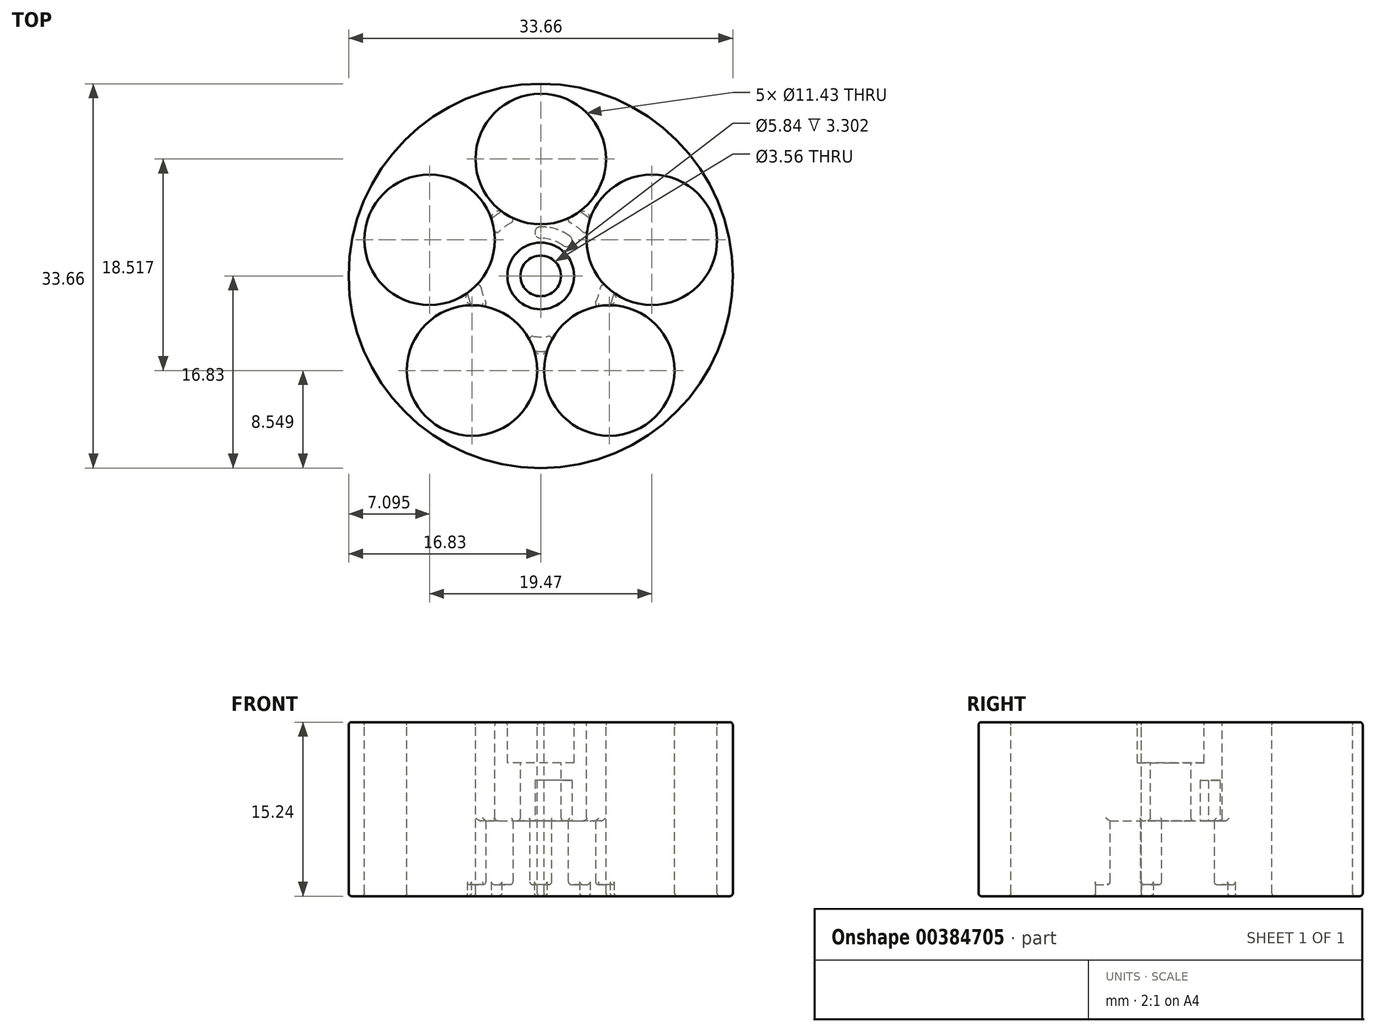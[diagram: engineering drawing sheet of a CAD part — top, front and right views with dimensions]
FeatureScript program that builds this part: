
annotation { "Feature Type Name" : "Feature", "Feature Type Description" : "" }
export const myFeature = defineFeature(function(context is Context, id is Id, definition is map)
    precondition{}
    {
        {
            var Q0;
            Q0=qCreatedBy(makeId("Top.planeOp"),FACE);
            var sketch = newSketch(context, id + "F0", { "sketchPlane" : qUnion([Q0])});
            skCircle(sketch, "E0", {"center": v(0, 0) * mm, "radius": 16.83 * mm});
            skSolve(sketch);
        }
        {
            var Q0;
            Q0=qSketchRegion(id+"F0",true);
            extrude(context, id + "F1", {"entities" : qUnion([Q0]), "depth" : 15.24 * mm, "offsetDistance" : 25.4 * mm});
        }
        {
            var Q0;
            Q0=makeQuery(id+"F1.opExtrude","CAP_FACE",FACE,{"disambiguationData":[OSD([sQuery(id+"F0.wireOp",EDGE,"E0")])],"isStart":false});
            var sketch = newSketch(context, id + "F2", { "sketchPlane" : qUnion([Q0])});
            skCircle(sketch, "E1", {"center": v(0, 10.24) * mm, "radius": 5.72 * mm});
            skCircle(sketch, "E2.1.0", {"center": v(-9.74, 3.16) * mm, "radius": 5.72 * mm});
            skCircle(sketch, "E2.2.0", {"center": v(-6.02, -8.28) * mm, "radius": 5.72 * mm});
            skCircle(sketch, "E2.3.0", {"center": v(6.02, -8.28) * mm, "radius": 5.72 * mm});
            skCircle(sketch, "E2.4.0", {"center": v(9.74, 3.16) * mm, "radius": 5.72 * mm});
            skPoint(sketch, "E2.center", {"position": v(0, 0) * mm});
            skSolve(sketch);
        }
        {
            var Q0;
            Q0=qSketchRegion(id+"F2",true);
            extrude(context, id + "F3", {"entities" : qUnion([Q0]), "operationType" : NewBodyOperationType.REMOVE, "oppositeDirection" : true, "depth" : 15.24 * mm});
        }
        {
            var Q0;
            Q0=makeQuery(id+"F1.opExtrude","CAP_FACE",FACE,{"disambiguationData":[OSD([sQuery(id+"F0.wireOp",EDGE,"E0")])],"isStart":true});
            var sketch = newSketch(context, id + "F4", { "sketchPlane" : qUnion([Q0])});
            skCircle(sketch, "E3", {"center": v(0, 0) * mm, "radius": 5.33 * mm});
            skSolve(sketch);
        }
        {
            var Q0;
            Q0=qSketchRegion(id+"F4",true);
            extrude(context, id + "F5", {"entities" : qUnion([Q0]), "operationType" : NewBodyOperationType.REMOVE, "oppositeDirection" : true, "depth" : 6.6 * mm, "offsetDistance" : 25.4 * mm});
        }
        {
            var Q0;
            Q0=makeQuery(id+"F1.opExtrude","CAP_FACE",FACE,{"disambiguationData":[OSD([sQuery(id+"F0.wireOp",EDGE,"E0")])],"isStart":false});
            var sketch = newSketch(context, id + "F6", { "sketchPlane" : qUnion([Q0])});
            skCircle(sketch, "E4", {"center": v(0, 0) * mm, "radius": 2.92 * mm});
            skSolve(sketch);
        }
        {
            var Q0;
            Q0=qSketchRegion(id+"F6",true);
            extrude(context, id + "F7", {"entities" : qUnion([Q0]), "operationType" : NewBodyOperationType.REMOVE, "oppositeDirection" : true, "depth" : 3.56 * mm});
        }
        {
            var Q0;
            Q0=makeQuery(id+"F7.boolean.opBoolean","COPY",FACE,{"derivedFrom":makeQuery(id+"F7.opExtrude","CAP_FACE",FACE,{"disambiguationData":[OSD([sQuery(id+"F6.wireOp",EDGE,"E4")])],"isStart":false})});
            var sketch = newSketch(context, id + "F8", { "sketchPlane" : qUnion([Q0])});
            skCircle(sketch, "E5", {"center": v(0, 0) * mm, "radius": 1.78 * mm});
            skSolve(sketch);
        }
        {
            var Q0;
            Q0=qSketchRegion(id+"F8",true);
            extrude(context, id + "F9", {"entities" : qUnion([Q0]), "operationType" : NewBodyOperationType.REMOVE, "oppositeDirection" : true, "depth" : 25.4 * mm});
        }
        {
            var Q0;
            Q0=makeQuery(id+"F1.opExtrude","CAP_FACE",FACE,{"disambiguationData":[OSD([sQuery(id+"F0.wireOp",EDGE,"E0")])],"isStart":true});
            var sketch = newSketch(context, id + "F10", { "sketchPlane" : qUnion([Q0])});
            skSolve(sketch);
        }
        {
            var Q0;
            {var subQ0=sQuery(id+"F0.wireOp",EDGE,"E0");Q0=makeQuery(id+"F10.imprint","IMPRINT",FACE,{"disambiguationData":[TD([[makeQuery(id+"F10.imprint","IMPRINT",EDGE,{"derivedFrom":makeQuery(id+"F1.opExtrude","CAP_EDGE",EDGE,{"disambiguationData":[OSD([subQ0])],"isStart":true})}),-1.0]])]});}
            var sketch = newSketch(context, id + "F11", { "sketchPlane" : qUnion([Q0])});
            skCircle(sketch, "E6", {"center": v(0, 0) * mm, "radius": 6.6 * mm});
            skSolve(sketch);
        }
        {
            var Q0;
            Q0=qSketchRegion(id+"F11",true);
            extrude(context, id + "F12", {"entities" : qUnion([Q0]), "operationType" : NewBodyOperationType.REMOVE, "oppositeDirection" : true, "depth" : 1.02 * mm, "offsetDistance" : 25.4 * mm});
        }
        {
            var Q0;
            Q0=qCreatedBy(makeId("Top.planeOp"),FACE);
            var sketch = newSketch(context, id + "F13", { "sketchPlane" : qUnion([Q0])});
            skArc(sketch, "E7", {"start": v(0, 4.32) * mm, "mid": v(-0.5, 3.81) * mm, "end": v(0, 3.3) * mm});
            skArc(sketch, "E8", {"start": v(1.94, 2.67) * mm, "mid": v(2.65, 2.78) * mm, "end": v(2.54, 3.5) * mm});
            skArc(sketch, "E9", {"start": v(1.94, 2.67) * mm, "mid": v(1.02, 3.14) * mm, "end": v(0, 3.3) * mm});
            skArc(sketch, "E10", {"start": v(2.54, 3.5) * mm, "mid": v(1.33, 4.1) * mm, "end": v(0, 4.32) * mm});
            skPoint(sketch, "E11.trimOffspring.end.orphan", {"position": v(6.02, -8.28) * mm});
            skSolve(sketch);
        }
        {
            var Q0;
            Q0=qSketchRegion(id+"F13",true);
            extrude(context, id + "F14", {"entities" : qUnion([Q0]), "operationType" : NewBodyOperationType.REMOVE, "depth" : 10.16 * mm, "offsetDistance" : 25.4 * mm});
        }
        {
            var Q0;
            Q0=makeQuery(id+"F1.opExtrude","CAP_FACE",FACE,{"disambiguationData":[OSD([sQuery(id+"F0.wireOp",EDGE,"E0")])],"isStart":false});
            var Q1;
            Q1=makeQuery(id+"F1.opExtrude","CAP_FACE",FACE,{"disambiguationData":[OSD([sQuery(id+"F0.wireOp",EDGE,"E0")])],"isStart":true});
            fillet(context, id + "F15", {"entities" : qUnion([Q0, Q1]), "radius" : 0.25 * mm, "tangentPropagation" : true, "allowEdgeOverflow" : false});
        }
        {
            var Q0;
            Q0=makeQuery(id+"F5.boolean.opBoolean","INTERSECT",EDGE,{"disambiguationData":[OD(0.0)],"derivedFrom":[makeQuery(id+"F3.boolean.opBoolean","COPY",FACE,{"derivedFrom":makeQuery(id+"F3.opExtrude","SWEPT_FACE",FACE,{"disambiguationData":[OSD([sQuery(id+"F2.wireOp",EDGE,"E2.3.0")])]})}),makeQuery(id+"F5.opExtrude","SWEPT_FACE",FACE,{"disambiguationData":[OSD([sQuery(id+"F4.wireOp",EDGE,"E3")])]})]});
            var Q1;
            Q1=makeQuery(id+"F5.boolean.opBoolean","INTERSECT",EDGE,{"disambiguationData":[OD(1.0)],"derivedFrom":[makeQuery(id+"F3.boolean.opBoolean","COPY",FACE,{"derivedFrom":makeQuery(id+"F3.opExtrude","SWEPT_FACE",FACE,{"disambiguationData":[OSD([sQuery(id+"F2.wireOp",EDGE,"E2.2.0")])]})}),makeQuery(id+"F5.opExtrude","SWEPT_FACE",FACE,{"disambiguationData":[OSD([sQuery(id+"F4.wireOp",EDGE,"E3")])]})]});
            var Q2;
            Q2=makeQuery(id+"F5.boolean.opBoolean","INTERSECT",EDGE,{"disambiguationData":[OD(0.0)],"derivedFrom":[makeQuery(id+"F3.boolean.opBoolean","COPY",FACE,{"derivedFrom":makeQuery(id+"F3.opExtrude","SWEPT_FACE",FACE,{"disambiguationData":[OSD([sQuery(id+"F2.wireOp",EDGE,"E2.2.0")])]})}),makeQuery(id+"F5.opExtrude","SWEPT_FACE",FACE,{"disambiguationData":[OSD([sQuery(id+"F4.wireOp",EDGE,"E3")])]})]});
            var Q3;
            Q3=makeQuery(id+"F5.boolean.opBoolean","INTERSECT",EDGE,{"disambiguationData":[OD(1.0)],"derivedFrom":[makeQuery(id+"F3.boolean.opBoolean","COPY",FACE,{"derivedFrom":makeQuery(id+"F3.opExtrude","SWEPT_FACE",FACE,{"disambiguationData":[OSD([sQuery(id+"F2.wireOp",EDGE,"E2.1.0")])]})}),makeQuery(id+"F5.opExtrude","SWEPT_FACE",FACE,{"disambiguationData":[OSD([sQuery(id+"F4.wireOp",EDGE,"E3")])]})]});
            var Q4;
            Q4=makeQuery(id+"F5.boolean.opBoolean","INTERSECT",EDGE,{"disambiguationData":[OD(1.0)],"derivedFrom":[makeQuery(id+"F3.boolean.opBoolean","COPY",FACE,{"derivedFrom":makeQuery(id+"F3.opExtrude","SWEPT_FACE",FACE,{"disambiguationData":[OSD([sQuery(id+"F2.wireOp",EDGE,"E2.4.0")])]})}),makeQuery(id+"F5.opExtrude","SWEPT_FACE",FACE,{"disambiguationData":[OSD([sQuery(id+"F4.wireOp",EDGE,"E3")])]})]});
            var Q5;
            Q5=makeQuery(id+"F5.boolean.opBoolean","INTERSECT",EDGE,{"disambiguationData":[OD(1.0)],"derivedFrom":[makeQuery(id+"F3.boolean.opBoolean","COPY",FACE,{"derivedFrom":makeQuery(id+"F3.opExtrude","SWEPT_FACE",FACE,{"disambiguationData":[OSD([sQuery(id+"F2.wireOp",EDGE,"E2.3.0")])]})}),makeQuery(id+"F5.opExtrude","SWEPT_FACE",FACE,{"disambiguationData":[OSD([sQuery(id+"F4.wireOp",EDGE,"E3")])]})]});
            var Q6;
            Q6=makeQuery(id+"F5.boolean.opBoolean","INTERSECT",EDGE,{"disambiguationData":[OD(0.0)],"derivedFrom":[makeQuery(id+"F3.boolean.opBoolean","COPY",FACE,{"derivedFrom":makeQuery(id+"F3.opExtrude","SWEPT_FACE",FACE,{"disambiguationData":[OSD([sQuery(id+"F2.wireOp",EDGE,"E2.4.0")])]})}),makeQuery(id+"F5.opExtrude","SWEPT_FACE",FACE,{"disambiguationData":[OSD([sQuery(id+"F4.wireOp",EDGE,"E3")])]})]});
            var Q7;
            Q7=makeQuery(id+"F5.boolean.opBoolean","INTERSECT",EDGE,{"disambiguationData":[OD(1.0)],"derivedFrom":[makeQuery(id+"F3.boolean.opBoolean","COPY",FACE,{"derivedFrom":makeQuery(id+"F3.opExtrude","SWEPT_FACE",FACE,{"disambiguationData":[OSD([sQuery(id+"F2.wireOp",EDGE,"E1")])]})}),makeQuery(id+"F5.opExtrude","SWEPT_FACE",FACE,{"disambiguationData":[OSD([sQuery(id+"F4.wireOp",EDGE,"E3")])]})]});
            var Q8;
            Q8=makeQuery(id+"F5.boolean.opBoolean","INTERSECT",EDGE,{"disambiguationData":[OD(0.0)],"derivedFrom":[makeQuery(id+"F3.boolean.opBoolean","COPY",FACE,{"derivedFrom":makeQuery(id+"F3.opExtrude","SWEPT_FACE",FACE,{"disambiguationData":[OSD([sQuery(id+"F2.wireOp",EDGE,"E2.1.0")])]})}),makeQuery(id+"F5.opExtrude","SWEPT_FACE",FACE,{"disambiguationData":[OSD([sQuery(id+"F4.wireOp",EDGE,"E3")])]})]});
            var Q9;
            Q9=makeQuery(id+"F5.boolean.opBoolean","INTERSECT",EDGE,{"disambiguationData":[OD(0.0)],"derivedFrom":[makeQuery(id+"F3.boolean.opBoolean","COPY",FACE,{"derivedFrom":makeQuery(id+"F3.opExtrude","SWEPT_FACE",FACE,{"disambiguationData":[OSD([sQuery(id+"F2.wireOp",EDGE,"E1")])]})}),makeQuery(id+"F5.opExtrude","SWEPT_FACE",FACE,{"disambiguationData":[OSD([sQuery(id+"F4.wireOp",EDGE,"E3")])]})]});
            var Q10;
            Q10=makeQuery(id+"F5.boolean.opBoolean","INTERSECT",EDGE,{"derivedFrom":[makeQuery(id+"F3.boolean.opBoolean","COPY",FACE,{"derivedFrom":makeQuery(id+"F3.opExtrude","SWEPT_FACE",FACE,{"disambiguationData":[OSD([sQuery(id+"F2.wireOp",EDGE,"E2.1.0")])]})}),makeQuery(id+"F5.opExtrude","CAP_FACE",FACE,{"disambiguationData":[OSD([sQuery(id+"F4.wireOp",EDGE,"E3")])],"isStart":false})]});
            var Q11;
            Q11=makeQuery(id+"F5.boolean.opBoolean","INTERSECT",EDGE,{"derivedFrom":[makeQuery(id+"F3.boolean.opBoolean","COPY",FACE,{"derivedFrom":makeQuery(id+"F3.opExtrude","SWEPT_FACE",FACE,{"disambiguationData":[OSD([sQuery(id+"F2.wireOp",EDGE,"E2.2.0")])]})}),makeQuery(id+"F5.opExtrude","CAP_FACE",FACE,{"disambiguationData":[OSD([sQuery(id+"F4.wireOp",EDGE,"E3")])],"isStart":false})]});
            var Q12;
            Q12=makeQuery(id+"F5.boolean.opBoolean","INTERSECT",EDGE,{"derivedFrom":[makeQuery(id+"F3.boolean.opBoolean","COPY",FACE,{"derivedFrom":makeQuery(id+"F3.opExtrude","SWEPT_FACE",FACE,{"disambiguationData":[OSD([sQuery(id+"F2.wireOp",EDGE,"E2.3.0")])]})}),makeQuery(id+"F5.opExtrude","CAP_FACE",FACE,{"disambiguationData":[OSD([sQuery(id+"F4.wireOp",EDGE,"E3")])],"isStart":false})]});
            var Q13;
            Q13=makeQuery(id+"F5.boolean.opBoolean","INTERSECT",EDGE,{"derivedFrom":[makeQuery(id+"F3.boolean.opBoolean","COPY",FACE,{"derivedFrom":makeQuery(id+"F3.opExtrude","SWEPT_FACE",FACE,{"disambiguationData":[OSD([sQuery(id+"F2.wireOp",EDGE,"E2.4.0")])]})}),makeQuery(id+"F5.opExtrude","CAP_FACE",FACE,{"disambiguationData":[OSD([sQuery(id+"F4.wireOp",EDGE,"E3")])],"isStart":false})]});
            var Q14;
            Q14=makeQuery(id+"F5.boolean.opBoolean","INTERSECT",EDGE,{"derivedFrom":[makeQuery(id+"F3.boolean.opBoolean","COPY",FACE,{"derivedFrom":makeQuery(id+"F3.opExtrude","SWEPT_FACE",FACE,{"disambiguationData":[OSD([sQuery(id+"F2.wireOp",EDGE,"E1")])]})}),makeQuery(id+"F5.opExtrude","CAP_FACE",FACE,{"disambiguationData":[OSD([sQuery(id+"F4.wireOp",EDGE,"E3")])],"isStart":false})]});
            var Q15;
            Q15=makeQuery(id+"F9.boolean.opBoolean","INTERSECT",EDGE,{"derivedFrom":[makeQuery(id+"F5.boolean.opBoolean","COPY",FACE,{"derivedFrom":makeQuery(id+"F5.opExtrude","CAP_FACE",FACE,{"disambiguationData":[OSD([sQuery(id+"F4.wireOp",EDGE,"E3")])],"isStart":false})}),makeQuery(id+"F9.opExtrude","SWEPT_FACE",FACE,{"disambiguationData":[OSD([sQuery(id+"F8.wireOp",EDGE,"E5")])]})]});
            var Q16;
            Q16=makeQuery(id+"F9.boolean.opBoolean","COPY",EDGE,{"derivedFrom":makeQuery(id+"F9.opExtrude","CAP_EDGE",EDGE,{"disambiguationData":[OSD([sQuery(id+"F8.wireOp",EDGE,"E5")])],"isStart":true})});
            var Q17;
            Q17=makeQuery(id+"F12.boolean.opBoolean","INTERSECT",EDGE,{"disambiguationData":[OD(1.0)],"derivedFrom":[makeQuery(id+"F3.boolean.opBoolean","COPY",FACE,{"derivedFrom":makeQuery(id+"F3.opExtrude","SWEPT_FACE",FACE,{"disambiguationData":[OSD([sQuery(id+"F2.wireOp",EDGE,"E2.1.0")])]})}),makeQuery(id+"F12.opExtrude","CAP_FACE",FACE,{"disambiguationData":[OSD([sQuery(id+"F11.wireOp",EDGE,"E6")])],"isStart":false})]});
            var Q18;
            Q18=makeQuery(id+"F12.boolean.opBoolean","INTERSECT",EDGE,{"disambiguationData":[OD(0.0)],"derivedFrom":[makeQuery(id+"F3.boolean.opBoolean","COPY",FACE,{"derivedFrom":makeQuery(id+"F3.opExtrude","SWEPT_FACE",FACE,{"disambiguationData":[OSD([sQuery(id+"F2.wireOp",EDGE,"E2.2.0")])]})}),makeQuery(id+"F12.opExtrude","CAP_FACE",FACE,{"disambiguationData":[OSD([sQuery(id+"F11.wireOp",EDGE,"E6")])],"isStart":false})]});
            var Q19;
            {var subQ0=sQuery(id+"F4.wireOp",EDGE,"E3");Q19=makeQuery(id+"F12.boolean.opBoolean","INTERSECT",EDGE,{"derivedFrom":[makeQuery(id+"F5.boolean.opBoolean","COPY",FACE,{"disambiguationData":[TD([makeQuery(id+"F1.opExtrude","CAP_FACE",FACE,{"disambiguationData":[OSD([sQuery(id+"F0.wireOp",EDGE,"E0")])],"isStart":true}),makeQuery(id+"F3.boolean.opBoolean","COPY",FACE,{"derivedFrom":makeQuery(id+"F3.opExtrude","SWEPT_FACE",FACE,{"disambiguationData":[OSD([sQuery(id+"F2.wireOp",EDGE,"E2.1.0")])]})}),makeQuery(id+"F3.boolean.opBoolean","COPY",FACE,{"derivedFrom":makeQuery(id+"F3.opExtrude","SWEPT_FACE",FACE,{"disambiguationData":[OSD([sQuery(id+"F2.wireOp",EDGE,"E2.2.0")])]})}),makeQuery(id+"F5.opExtrude","CAP_FACE",FACE,{"disambiguationData":[OSD([subQ0])],"isStart":false})])],"derivedFrom":makeQuery(id+"F5.opExtrude","SWEPT_FACE",FACE,{"disambiguationData":[OSD([subQ0])]})}),makeQuery(id+"F12.opExtrude","CAP_FACE",FACE,{"disambiguationData":[OSD([sQuery(id+"F11.wireOp",EDGE,"E6")])],"isStart":false})]});}
            var Q20;
            Q20=makeQuery(id+"F12.boolean.opBoolean","INTERSECT",EDGE,{"disambiguationData":[OD(1.0)],"derivedFrom":[makeQuery(id+"F3.boolean.opBoolean","COPY",FACE,{"derivedFrom":makeQuery(id+"F3.opExtrude","SWEPT_FACE",FACE,{"disambiguationData":[OSD([sQuery(id+"F2.wireOp",EDGE,"E2.2.0")])]})}),makeQuery(id+"F12.opExtrude","CAP_FACE",FACE,{"disambiguationData":[OSD([sQuery(id+"F11.wireOp",EDGE,"E6")])],"isStart":false})]});
            var Q21;
            {var subQ0=sQuery(id+"F4.wireOp",EDGE,"E3");Q21=makeQuery(id+"F12.boolean.opBoolean","INTERSECT",EDGE,{"derivedFrom":[makeQuery(id+"F5.boolean.opBoolean","COPY",FACE,{"disambiguationData":[TD([makeQuery(id+"F1.opExtrude","CAP_FACE",FACE,{"disambiguationData":[OSD([sQuery(id+"F0.wireOp",EDGE,"E0")])],"isStart":true}),makeQuery(id+"F3.boolean.opBoolean","COPY",FACE,{"derivedFrom":makeQuery(id+"F3.opExtrude","SWEPT_FACE",FACE,{"disambiguationData":[OSD([sQuery(id+"F2.wireOp",EDGE,"E2.2.0")])]})}),makeQuery(id+"F3.boolean.opBoolean","COPY",FACE,{"derivedFrom":makeQuery(id+"F3.opExtrude","SWEPT_FACE",FACE,{"disambiguationData":[OSD([sQuery(id+"F2.wireOp",EDGE,"E2.3.0")])]})}),makeQuery(id+"F5.opExtrude","CAP_FACE",FACE,{"disambiguationData":[OSD([subQ0])],"isStart":false})])],"derivedFrom":makeQuery(id+"F5.opExtrude","SWEPT_FACE",FACE,{"disambiguationData":[OSD([subQ0])]})}),makeQuery(id+"F12.opExtrude","CAP_FACE",FACE,{"disambiguationData":[OSD([sQuery(id+"F11.wireOp",EDGE,"E6")])],"isStart":false})]});}
            var Q22;
            Q22=makeQuery(id+"F12.boolean.opBoolean","INTERSECT",EDGE,{"disambiguationData":[OD(0.0)],"derivedFrom":[makeQuery(id+"F3.boolean.opBoolean","COPY",FACE,{"derivedFrom":makeQuery(id+"F3.opExtrude","SWEPT_FACE",FACE,{"disambiguationData":[OSD([sQuery(id+"F2.wireOp",EDGE,"E2.3.0")])]})}),makeQuery(id+"F12.opExtrude","CAP_FACE",FACE,{"disambiguationData":[OSD([sQuery(id+"F11.wireOp",EDGE,"E6")])],"isStart":false})]});
            var Q23;
            {var subQ0=sQuery(id+"F4.wireOp",EDGE,"E3");Q23=makeQuery(id+"F12.boolean.opBoolean","INTERSECT",EDGE,{"derivedFrom":[makeQuery(id+"F5.boolean.opBoolean","COPY",FACE,{"disambiguationData":[TD([makeQuery(id+"F1.opExtrude","CAP_FACE",FACE,{"disambiguationData":[OSD([sQuery(id+"F0.wireOp",EDGE,"E0")])],"isStart":true}),makeQuery(id+"F3.boolean.opBoolean","COPY",FACE,{"derivedFrom":makeQuery(id+"F3.opExtrude","SWEPT_FACE",FACE,{"disambiguationData":[OSD([sQuery(id+"F2.wireOp",EDGE,"E2.3.0")])]})}),makeQuery(id+"F3.boolean.opBoolean","COPY",FACE,{"derivedFrom":makeQuery(id+"F3.opExtrude","SWEPT_FACE",FACE,{"disambiguationData":[OSD([sQuery(id+"F2.wireOp",EDGE,"E2.4.0")])]})}),makeQuery(id+"F5.opExtrude","CAP_FACE",FACE,{"disambiguationData":[OSD([subQ0])],"isStart":false})])],"derivedFrom":makeQuery(id+"F5.opExtrude","SWEPT_FACE",FACE,{"disambiguationData":[OSD([subQ0])]})}),makeQuery(id+"F12.opExtrude","CAP_FACE",FACE,{"disambiguationData":[OSD([sQuery(id+"F11.wireOp",EDGE,"E6")])],"isStart":false})]});}
            var Q24;
            Q24=makeQuery(id+"F12.boolean.opBoolean","INTERSECT",EDGE,{"disambiguationData":[OD(1.0)],"derivedFrom":[makeQuery(id+"F3.boolean.opBoolean","COPY",FACE,{"derivedFrom":makeQuery(id+"F3.opExtrude","SWEPT_FACE",FACE,{"disambiguationData":[OSD([sQuery(id+"F2.wireOp",EDGE,"E2.4.0")])]})}),makeQuery(id+"F12.opExtrude","CAP_FACE",FACE,{"disambiguationData":[OSD([sQuery(id+"F11.wireOp",EDGE,"E6")])],"isStart":false})]});
            var Q25;
            Q25=makeQuery(id+"F12.boolean.opBoolean","INTERSECT",EDGE,{"disambiguationData":[OD(1.0)],"derivedFrom":[makeQuery(id+"F3.boolean.opBoolean","COPY",FACE,{"derivedFrom":makeQuery(id+"F3.opExtrude","SWEPT_FACE",FACE,{"disambiguationData":[OSD([sQuery(id+"F2.wireOp",EDGE,"E2.3.0")])]})}),makeQuery(id+"F12.opExtrude","CAP_FACE",FACE,{"disambiguationData":[OSD([sQuery(id+"F11.wireOp",EDGE,"E6")])],"isStart":false})]});
            var Q26;
            Q26=makeQuery(id+"F12.boolean.opBoolean","INTERSECT",EDGE,{"disambiguationData":[OD(1.0)],"derivedFrom":[makeQuery(id+"F3.boolean.opBoolean","COPY",FACE,{"derivedFrom":makeQuery(id+"F3.opExtrude","SWEPT_FACE",FACE,{"disambiguationData":[OSD([sQuery(id+"F2.wireOp",EDGE,"E1")])]})}),makeQuery(id+"F12.opExtrude","CAP_FACE",FACE,{"disambiguationData":[OSD([sQuery(id+"F11.wireOp",EDGE,"E6")])],"isStart":false})]});
            var Q27;
            {var subQ0=sQuery(id+"F4.wireOp",EDGE,"E3");Q27=makeQuery(id+"F12.boolean.opBoolean","INTERSECT",EDGE,{"derivedFrom":[makeQuery(id+"F5.boolean.opBoolean","COPY",FACE,{"disambiguationData":[TD([makeQuery(id+"F1.opExtrude","CAP_FACE",FACE,{"disambiguationData":[OSD([sQuery(id+"F0.wireOp",EDGE,"E0")])],"isStart":true}),makeQuery(id+"F3.boolean.opBoolean","COPY",FACE,{"derivedFrom":makeQuery(id+"F3.opExtrude","SWEPT_FACE",FACE,{"disambiguationData":[OSD([sQuery(id+"F2.wireOp",EDGE,"E1")])]})}),makeQuery(id+"F3.boolean.opBoolean","COPY",FACE,{"derivedFrom":makeQuery(id+"F3.opExtrude","SWEPT_FACE",FACE,{"disambiguationData":[OSD([sQuery(id+"F2.wireOp",EDGE,"E2.4.0")])]})}),makeQuery(id+"F5.opExtrude","CAP_FACE",FACE,{"disambiguationData":[OSD([subQ0])],"isStart":false})])],"derivedFrom":makeQuery(id+"F5.opExtrude","SWEPT_FACE",FACE,{"disambiguationData":[OSD([subQ0])]})}),makeQuery(id+"F12.opExtrude","CAP_FACE",FACE,{"disambiguationData":[OSD([sQuery(id+"F11.wireOp",EDGE,"E6")])],"isStart":false})]});}
            var Q28;
            Q28=makeQuery(id+"F12.boolean.opBoolean","INTERSECT",EDGE,{"disambiguationData":[OD(0.0)],"derivedFrom":[makeQuery(id+"F3.boolean.opBoolean","COPY",FACE,{"derivedFrom":makeQuery(id+"F3.opExtrude","SWEPT_FACE",FACE,{"disambiguationData":[OSD([sQuery(id+"F2.wireOp",EDGE,"E2.4.0")])]})}),makeQuery(id+"F12.opExtrude","CAP_FACE",FACE,{"disambiguationData":[OSD([sQuery(id+"F11.wireOp",EDGE,"E6")])],"isStart":false})]});
            var Q29;
            Q29=makeQuery(id+"F12.boolean.opBoolean","INTERSECT",EDGE,{"disambiguationData":[OD(0.0)],"derivedFrom":[makeQuery(id+"F3.boolean.opBoolean","COPY",FACE,{"derivedFrom":makeQuery(id+"F3.opExtrude","SWEPT_FACE",FACE,{"disambiguationData":[OSD([sQuery(id+"F2.wireOp",EDGE,"E2.1.0")])]})}),makeQuery(id+"F12.opExtrude","CAP_FACE",FACE,{"disambiguationData":[OSD([sQuery(id+"F11.wireOp",EDGE,"E6")])],"isStart":false})]});
            var Q30;
            {var subQ0=sQuery(id+"F4.wireOp",EDGE,"E3");Q30=makeQuery(id+"F12.boolean.opBoolean","INTERSECT",EDGE,{"derivedFrom":[makeQuery(id+"F5.boolean.opBoolean","COPY",FACE,{"disambiguationData":[TD([makeQuery(id+"F1.opExtrude","CAP_FACE",FACE,{"disambiguationData":[OSD([sQuery(id+"F0.wireOp",EDGE,"E0")])],"isStart":true}),makeQuery(id+"F3.boolean.opBoolean","COPY",FACE,{"derivedFrom":makeQuery(id+"F3.opExtrude","SWEPT_FACE",FACE,{"disambiguationData":[OSD([sQuery(id+"F2.wireOp",EDGE,"E1")])]})}),makeQuery(id+"F3.boolean.opBoolean","COPY",FACE,{"derivedFrom":makeQuery(id+"F3.opExtrude","SWEPT_FACE",FACE,{"disambiguationData":[OSD([sQuery(id+"F2.wireOp",EDGE,"E2.1.0")])]})}),makeQuery(id+"F5.opExtrude","CAP_FACE",FACE,{"disambiguationData":[OSD([subQ0])],"isStart":false})])],"derivedFrom":makeQuery(id+"F5.opExtrude","SWEPT_FACE",FACE,{"disambiguationData":[OSD([subQ0])]})}),makeQuery(id+"F12.opExtrude","CAP_FACE",FACE,{"disambiguationData":[OSD([sQuery(id+"F11.wireOp",EDGE,"E6")])],"isStart":false})]});}
            var Q31;
            Q31=makeQuery(id+"F12.boolean.opBoolean","INTERSECT",EDGE,{"disambiguationData":[OD(0.0)],"derivedFrom":[makeQuery(id+"F3.boolean.opBoolean","COPY",FACE,{"derivedFrom":makeQuery(id+"F3.opExtrude","SWEPT_FACE",FACE,{"disambiguationData":[OSD([sQuery(id+"F2.wireOp",EDGE,"E1")])]})}),makeQuery(id+"F12.opExtrude","CAP_FACE",FACE,{"disambiguationData":[OSD([sQuery(id+"F11.wireOp",EDGE,"E6")])],"isStart":false})]});
            fillet(context, id + "F16", {"entities" : qUnion([Q0, Q1, Q2, Q3, Q4, Q5, Q6, Q7, Q8, Q9, Q10, Q11, Q12, Q13, Q14, Q15, Q16, Q17, Q18, Q19, Q20, Q21, Q22, Q23, Q24, Q25, Q26, Q27, Q28, Q29, Q30, Q31]), "radius" : 0.25 * mm, "tangentPropagation" : true, "allowEdgeOverflow" : false});
        }
    });
